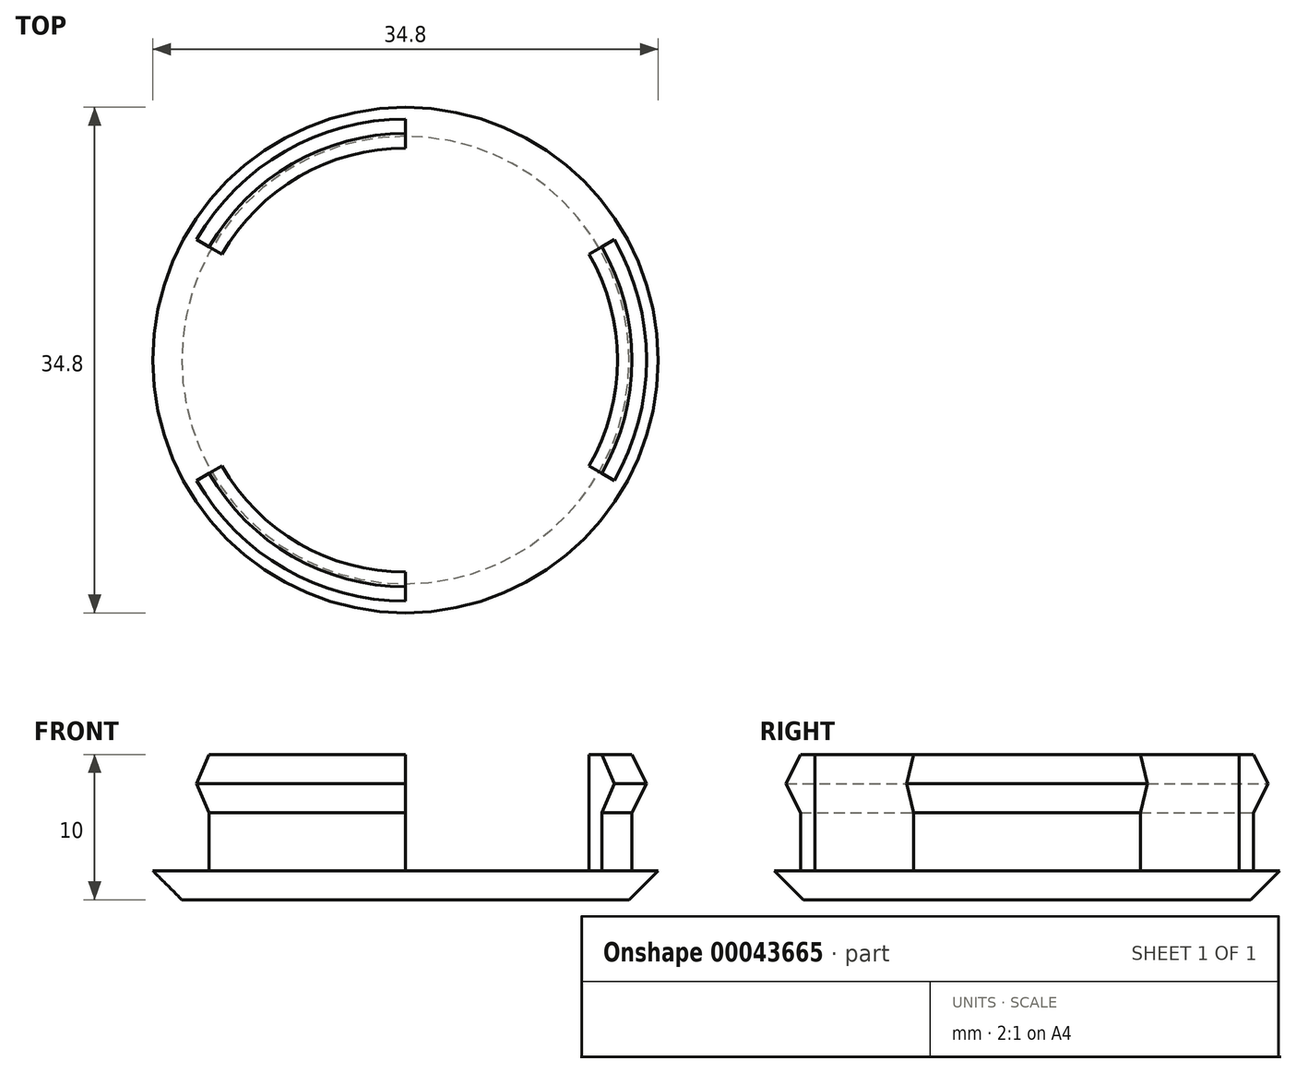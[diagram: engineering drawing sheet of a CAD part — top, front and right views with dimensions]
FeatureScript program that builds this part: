
annotation { "Feature Type Name" : "Feature", "Feature Type Description" : "" }
export const myFeature = defineFeature(function(context is Context, id is Id, definition is map)
    precondition{}
    {
        {
            var Q0;
            Q0=qCreatedBy(makeId("Front.planeOp"),FACE);
            var sketch = newSketch(context, id + "F0", { "sketchPlane" : qUnion([Q0])});
            skLineSegment(sketch, "E0.bottom", {"start": v(0, 0) * mm, "end": v(15.4, 0) * mm});
            skLineSegment(sketch, "E0.top", {"start": v(0, 2) * mm, "end": v(15.4, 2) * mm});
            skLineSegment(sketch, "E0.left", {"start": v(0, 0) * mm, "end": v(0, 2) * mm});
            skLineSegment(sketch, "E0.right", {"start": v(15.4, 0) * mm, "end": v(15.4, 2) * mm});
            skLineSegment(sketch, "E1.bottom", {"start": v(15.6, 2) * mm, "end": v(15.4, 2) * mm});
            skLineSegment(sketch, "E1.top", {"start": v(15.6, 10) * mm, "end": v(14.6, 10) * mm});
            skLineSegment(sketch, "E1.left", {"start": v(14.6, 2) * mm, "end": v(14.6, 10) * mm});
            skLineSegment(sketch, "E1.right", {"start": v(15.6, 2) * mm, "end": v(15.6, 10) * mm});
            skLineSegment(sketch, "E2", {"start": v(15.4, 0) * mm, "end": v(17.4, 2) * mm});
            skLineSegment(sketch, "E3", {"start": v(17.4, 2) * mm, "end": v(15.4, 2) * mm});
            skLineSegment(sketch, "E4", {"start": v(15.6, 10) * mm, "end": v(16.6, 8) * mm});
            skLineSegment(sketch, "E5", {"start": v(16.6, 8) * mm, "end": v(15.6, 6) * mm});
            skLineSegment(sketch, "E6", {"start": v(15.6, 8) * mm, "end": v(16.6, 8) * mm, "construction": true});
            skLineSegment(sketch, "E7", {"start": v(0, 0) * mm, "end": v(0, 4.16) * mm, "construction": true});
            skLineSegment(sketch, "E8", {"start": v(0, 4.16) * mm, "end": v(15.6, 4.16) * mm, "construction": true});
            skSolve(sketch);
        }
        {
            var Q0;
            Q0 = qSketchRegion(id + "F0", true);
            var Q1;
            Q1=sQuery(id+"F0.wireOp",EDGE,"E0.left");
            revolve(context, id + "F1", {"entities" : qUnion([Q0]), "axis" : qUnion([Q1]), "revolveType" : RevolveType.FULL});
        }
        {
            var Q0;
            Q0=makeQuery(id+"F1.opRevolve","SWEPT_FACE",FACE,{"disambiguationData":[OSD([sQuery(id+"F0.wireOp",EDGE,"E0.top")])]});
            var sketch = newSketch(context, id + "F2", { "sketchPlane" : qUnion([Q0])});
            skLineSegment(sketch, "E9", {"start": v(0, 0) * mm, "end": v(0, 19) * mm});
            skLineSegment(sketch, "E10", {"start": v(16.45, 9.5) * mm, "end": v(0, 0) * mm});
            skArc(sketch, "E11", {"start": v(16.45, 9.5) * mm, "mid": v(9.5, 16.45) * mm, "end": v(0, 19) * mm});
            skLineSegment(sketch, "E12.1.0", {"start": v(0, 0) * mm, "end": v(-16.45, -9.5) * mm});
            skArc(sketch, "E12.1.1", {"start": v(-16.45, 9.5) * mm, "mid": v(-19, 0) * mm, "end": v(-16.45, -9.5) * mm});
            skLineSegment(sketch, "E12.1.2", {"start": v(-16.45, 9.5) * mm, "end": v(0, 0) * mm});
            skLineSegment(sketch, "E12.2.0", {"start": v(0, 0) * mm, "end": v(16.45, -9.5) * mm});
            skArc(sketch, "E12.2.1", {"start": v(0, -19) * mm, "mid": v(9.5, -16.45) * mm, "end": v(16.45, -9.5) * mm});
            skLineSegment(sketch, "E12.2.2", {"start": v(0, -19) * mm, "end": v(0, 0) * mm});
            skSolve(sketch);
        }
        {
            var Q0;
            Q0 = qSketchRegion(id + "F2", true);
            extrude(context, id + "F3", {"entities" : qUnion([Q0]), "operationType" : NewBodyOperationType.REMOVE, "endBound" : BoundingType.THROUGH_ALL, "depth" : 25 * mm});
        }
    });
